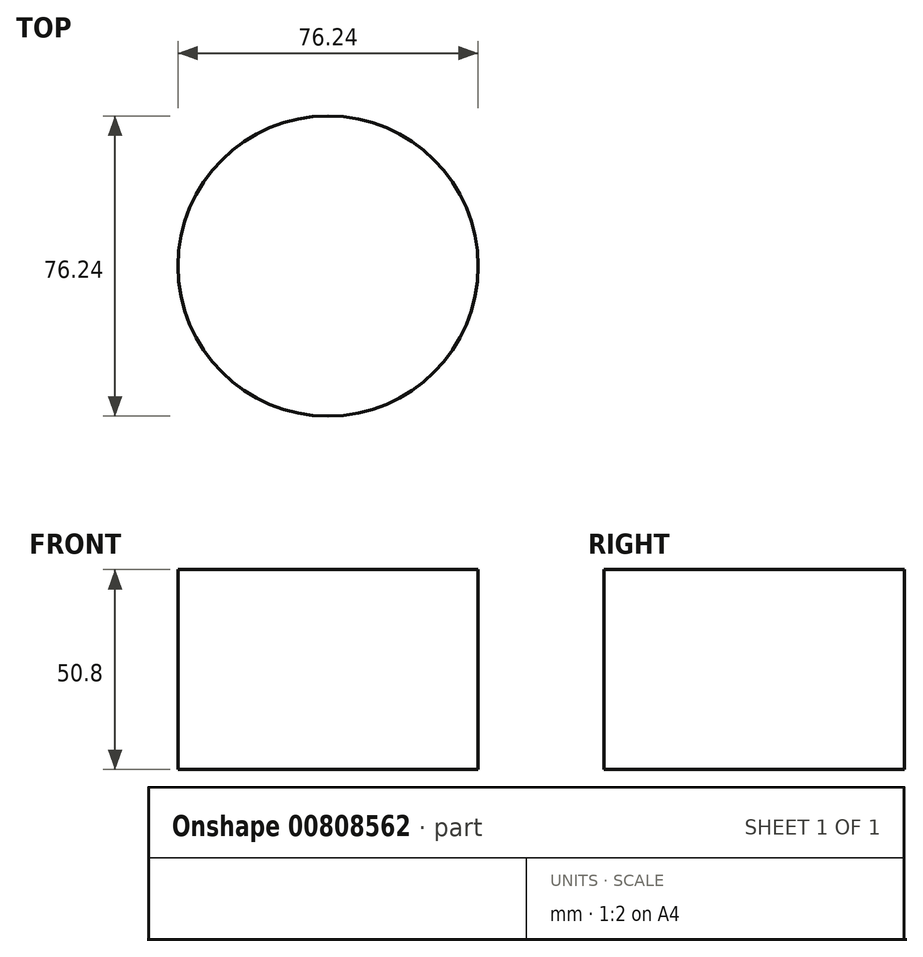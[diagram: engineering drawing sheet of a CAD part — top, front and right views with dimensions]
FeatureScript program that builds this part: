
annotation { "Feature Type Name" : "Feature", "Feature Type Description" : "" }
export const myFeature = defineFeature(function(context is Context, id is Id, definition is map)
    precondition{}
    {
        {
            var Q0;
            Q0=qCreatedBy(makeId("Top.planeOp"),FACE);
            var sketch = newSketch(context, id + "F0", { "sketchPlane" : qUnion([Q0])});
            skLineSegment(sketch, "E0", {"start": v(0, 0) * mm, "end": v(0, 38.25) * mm});
            skLineSegment(sketch, "E1", {"start": v(0, 0) * mm, "end": v(0, -38.12) * mm});
            skLineSegment(sketch, "E2", {"start": v(0, 0) * mm, "end": v(-38.12, 0) * mm});
            skLineSegment(sketch, "E3", {"start": v(0, 0) * mm, "end": v(38.12, 0) * mm});
            skCircle(sketch, "E4", {"center": v(0, 0) * mm, "radius": 38.12 * mm});
            skSolve(sketch);
        }
        {
            var Q0;
            {var subQ0=sQuery(id+"F0.wireOp",EDGE,"E1");Q0=makeQuery(id+"F0.imprint","IMPRINT",FACE,{"disambiguationData":[TD([[makeQuery(id+"F0.imprint","IMPRINT",EDGE,{"derivedFrom":subQ0}),-1.0]])]});}
            var Q1;
            {var subQ0=sQuery(id+"F0.wireOp",EDGE,"E2");Q1=makeQuery(id+"F0.imprint","IMPRINT",FACE,{"disambiguationData":[TD([[makeQuery(id+"F0.imprint","IMPRINT",EDGE,{"derivedFrom":subQ0}),-1.0]])]});}
            var Q2;
            {var subQ0=sQuery(id+"F0.wireOp",EDGE,"E1");Q2=makeQuery(id+"F0.imprint","IMPRINT",FACE,{"disambiguationData":[TD([[makeQuery(id+"F0.imprint","IMPRINT",EDGE,{"derivedFrom":subQ0}),1.0]])]});}
            var Q3;
            {var subQ0=sQuery(id+"F0.wireOp",EDGE,"E3");Q3=makeQuery(id+"F0.imprint","IMPRINT",FACE,{"disambiguationData":[TD([[makeQuery(id+"F0.imprint","IMPRINT",EDGE,{"derivedFrom":subQ0}),1.0]])]});}
            extrude(context, id + "F1", {"entities" : qUnion([Q0, Q1, Q2, Q3]), "oppositeDirection" : true, "depth" : 50.8 * mm, "offsetDistance" : 25.4 * mm});
        }
    });
